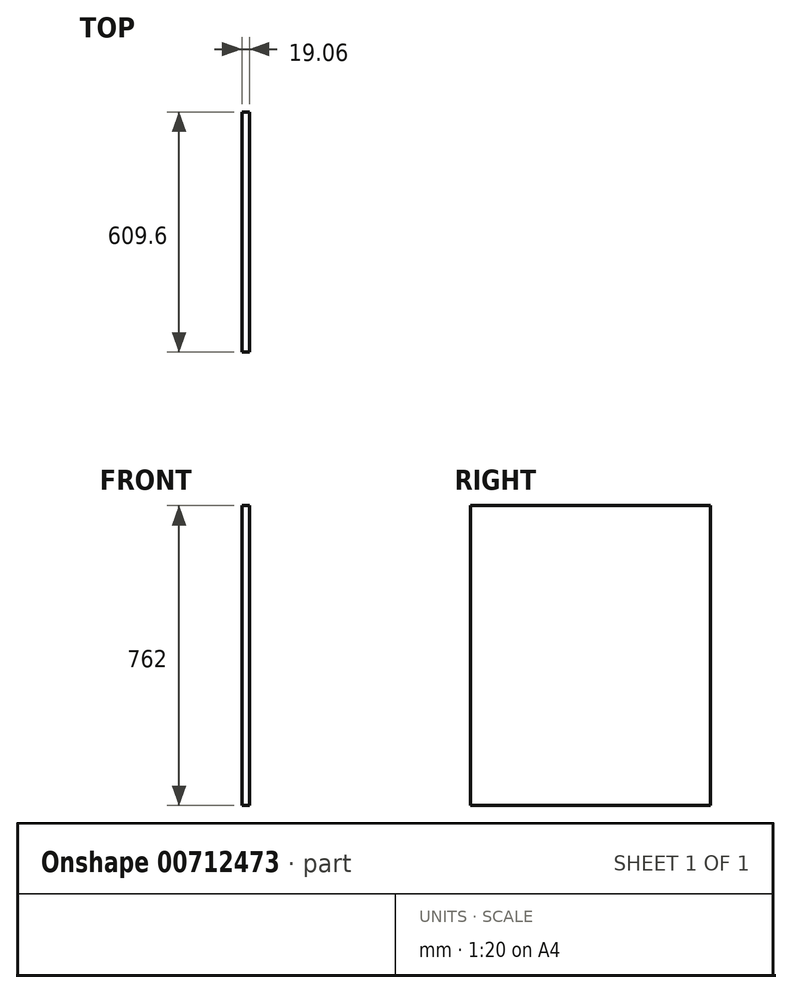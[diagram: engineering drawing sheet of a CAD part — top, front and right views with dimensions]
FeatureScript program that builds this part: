
annotation { "Feature Type Name" : "Feature", "Feature Type Description" : "" }
export const myFeature = defineFeature(function(context is Context, id is Id, definition is map)
    precondition{}
    {
        {
            var Q0;
            Q0=qCreatedBy(makeId("Right.planeOp"),FACE);
            var sketch = newSketch(context, id + "F0", { "sketchPlane" : qUnion([Q0])});
            skLineSegment(sketch, "E0.bottom", {"start": v(-304.8, 381) * mm, "end": v(304.8, 381) * mm});
            skLineSegment(sketch, "E0.top", {"start": v(-304.8, -381) * mm, "end": v(304.8, -381) * mm});
            skLineSegment(sketch, "E0.left", {"start": v(-304.8, 381) * mm, "end": v(-304.8, -381) * mm});
            skLineSegment(sketch, "E0.right", {"start": v(304.8, 381) * mm, "end": v(304.8, -381) * mm});
            skPoint(sketch, "E0.middle", {"position": v(0, 0) * mm});
            skSolve(sketch);
        }
        {
            var Q0;
            Q0 = qSketchRegion(id + "F0", true);
            extrude(context, id + "F1", {"entities" : qUnion([Q0]), "endBound" : BoundingType.SYMMETRIC, "depth" : 19.05 * mm, "offsetDistance" : 25.4 * mm});
        }
    });
